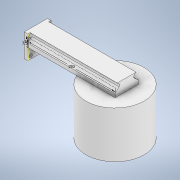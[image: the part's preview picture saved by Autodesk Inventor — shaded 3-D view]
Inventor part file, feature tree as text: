
AUTODESK INVENTOR PART (.ipt)
format: ipt  version: 2021.1 (Build 251245010, 245A)  size: 177,152 bytes
history: native  units: mm
features: sketch x6, extrude x5, plane x4, mirror x2
ambient origin geometry x8: Origin, YZ Plane, XZ Plane, XY Plane, X Axis, Y Axis, Z Axis, Center Point
bodies: Solid1 (feature_tree)
feature tree (17):
  extrude  "Extrusion1"  Depth=40.0mm
  extrude  "Extrusion2"  Depth=6.0mm
  mirror  "Mirror1"
  mirror  "Mirror2"
  plane  "Work Plane4"
  sketch  "Sketch3"  dims[d5=5.0mm d6=6.0mm]
  extrude  "Extrusion3"  Depth=6.0mm
  extrude  "Extrusion4"  [1 undecoded]
  extrude  "Extrusion5"  Depth=150.0mm
  sketch  "Sketch1"  dims[d0=40.0mm d1=40.0mm]
  sketch  "Sketch2"  dims[d2=6.0mm d3=0.0mm d4=5.0mm]
  plane  "Work Plane1"
  plane  "Work Plane2"
  plane  "Work Plane3"
  sketch  "Sketch4"  dims[d7=6.0mm d8=0.0mm d9=-20.0mm]
  sketch  "Sketch5"  dims[d10=15.0mm d11=150.0mm]
  sketch  "Sketch6"  dims[d12=7.5mm d13=150.0mm d14=0.0mm d15=10.0mm d16=60.0mm d17=40.0mm d20=0.0mm d21=93.0mm d22=70.0mm d23=0.0mm]
note: 1 required parameter value undecoded (feature->parameter linkage not recoverable at this tier; creation-order binding heuristic only, values carry confidence <= 0.55)
